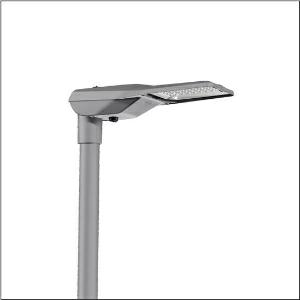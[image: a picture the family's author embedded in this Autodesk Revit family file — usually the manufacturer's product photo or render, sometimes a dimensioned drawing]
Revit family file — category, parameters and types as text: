
# Revit family: streetlight_sl_21_iq_mini___st1_0a_5xe2d31y08gb_99d1
name_source: partatom
category: Lighting Fixtures
units: mm (PartAtom-declared; Revit-internal decimal feet)

## family parameters
Cut with Voids When Loaded = No
Host = Face
Light Source = No
Part Type = Normal
Room Calculation Point = No
Round Connector Dimension = Use Diameter
Shared = No

## types (1)
- --- (1 x LED, 5990 lm, 39.8 W, 3000K)
    Apparent Load = 40 VA
    CIE Flux Codes = 37 72 97 100 100
    Color Rendering = 70
    Color Temperature = 3000K
    Default Elevation = 1800 mm
    Description = Streetlight SL 21 iQ mini, mast luminaire, primary light control with lens, of PMMA, primary optical cover: cover, of toughened safety glass, transparent, light distribution: ST1.0a, light emission: direct distribution, primary light characteristic: asymmetric, installation type: post-top, side-entry, LED, High Power LED, rated luminous flux: 5.990lm, luminous efficacy: 151lm/W, light colour: 730, colour temperature: 3000K, control: presetting dimming logarithmic, Street-Remote, Auto-Match, Temp-Guard, Lumen-Switch, Night-Set, Smart-Wire, Light-Fading, Desk-Remote (wireless, voltage-free reading and setting of iQ features in the workshop via application-optimized NFC function/RFID function), optimised constant luminous flux control (CLO 2.0), mains connection: 220..240V, AC, 50/60Hz, start of lifetime: 40W, end of service life: 41W, reduction: 18W, luminaire housing, of diecast aluminium, powder-coated, Siteco® metallic grey (DB 702S), corrosivity category C5 mid according to DIN EN ISO 12944, please order mast flange separately, inclination adjustable: 0°, 5°, 10°, 15°, sealing non-destructively replaceable, multi-level sealing system, length: 628mm, width: 235mm, height: 110mm, mast flange for spigot size: 42mm (side-entry): 5XC10008XM4, 60/48mm (side-entry/post-top): 5XC10108XM2, 76/60mm (side-entry/post-top): 5XC10108XM1, Smart Interface below and above, protection rating (complete): IP66, insulation class (complete): insulation class II (safety insulation), certification: CE, ENEC, ENEC+, VDE, impact resistance: IK09, permissible operating ambient temperature for outdoor applications: -40..+50°C, standard-compliant lighting for roads and squares, packaging unit: 1 piece

Light Distribution: ST1.0a
    Height = 110 mm
    Lamp = 1 x LED
    Lamp Light Flux = 5990 lm
    Lamp Power = 39.8 W
    Lamp count = 1
    Length = 625 mm
    Luminous efficacy = 151 lm/W
    Manufacturer = Siteco
    ModVariant = No
    Model = 5XE2D31Y08GB
    Number of Poles = 1
    OnlyDefault = Yes
    Power Factor = 1
    Product Name = Streetlight SL 21 iQ mini | ST1.0a
    Product group = mast luminaire | pylon top
    ProductGroupID = 6100
    Protection Class = Protection class II
    Protection Degree = IP 66
    RLX_Detail_Level = 1
    RLX_Emergency_Light_Flux = 0 lm
    RLX_Emergency_Type = 0
    RLX_Emergency_Type_DB = No
    RlxData = <blob elided: 92793 chars, md5=950039b2>
    Socket = socket
    Standby Power = 0 W
    System Light Flux = 5990 lm
    System Power = 40 W
    Type Comments = factory setting: luminous flux: 100 % | dim-lin: 254 | 800 mA
    Type Image = l_1003514.jpg
    URL = http://relux.com
    VarID = @adj_044953
    Voltage = 0 V
    Weight = 0.00 kg
    Width = 234 mm

## geometry (parser evidence)
native form markers: Blend x4, Sweep x11
no freeform markers — native parametric forms only
